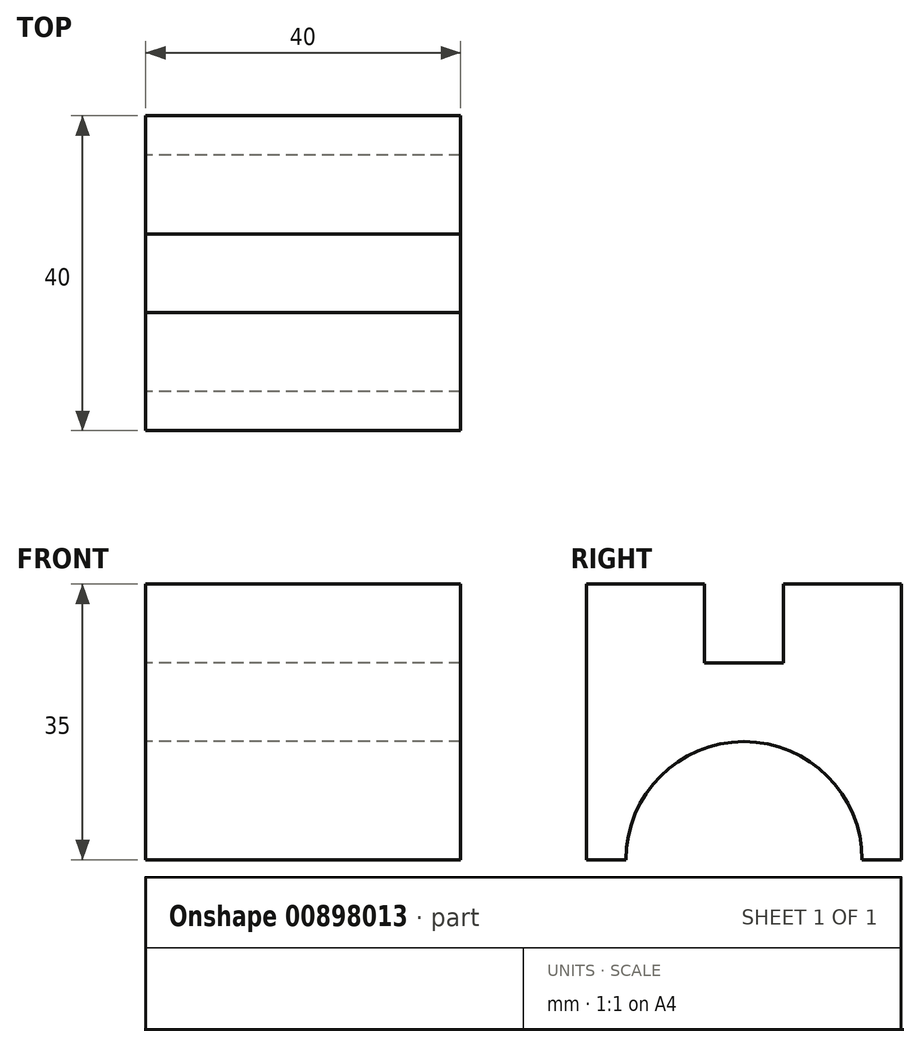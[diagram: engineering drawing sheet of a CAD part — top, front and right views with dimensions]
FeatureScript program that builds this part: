
annotation { "Feature Type Name" : "Feature", "Feature Type Description" : "" }
export const myFeature = defineFeature(function(context is Context, id is Id, definition is map)
    precondition{}
    {
        {
            var Q0;
            Q0=qCreatedBy(makeId("Front.planeOp"),FACE);
            var sketch = newSketch(context, id + "F0", { "sketchPlane" : qUnion([Q0])});
            skLineSegment(sketch, "E0.bottom", {"start": v(-20, 35) * mm, "end": v(20, 35) * mm});
            skLineSegment(sketch, "E0.top", {"start": v(-20, 0) * mm, "end": v(20, 0) * mm});
            skLineSegment(sketch, "E0.left", {"start": v(-20, 35) * mm, "end": v(-20, 0) * mm});
            skLineSegment(sketch, "E0.right", {"start": v(20, 35) * mm, "end": v(20, 0) * mm});
            skSolve(sketch);
        }
        {
            var Q0;
            Q0=makeQuery(id+"F0.imprint","IMPRINT",FACE,{"disambiguationData":[TD([[makeQuery(id+"F0.imprint","IMPRINT",EDGE,{"derivedFrom":sQuery(id+"F0.wireOp",EDGE,"E0.bottom")}),-1.0]])]});
            extrude(context, id + "F1", {"entities" : qUnion([Q0]), "endBound" : BoundingType.SYMMETRIC, "depth" : 40 * mm, "offsetDistance" : 25 * mm});
        }
        {
            var Q0;
            Q0=makeQuery(id+"F1.opExtrude","SWEPT_FACE",FACE,{"disambiguationData":[OSD([sQuery(id+"F0.wireOp",EDGE,"E0.left")])]});
            var sketch = newSketch(context, id + "F2", { "sketchPlane" : qUnion([Q0])});
            skCircle(sketch, "E1", {"center": v(0, 0) * mm, "radius": 15 * mm});
            skLineSegment(sketch, "E2.bottom", {"start": v(-5, 35) * mm, "end": v(5, 35) * mm});
            skLineSegment(sketch, "E2.top", {"start": v(-5, 25) * mm, "end": v(5, 25) * mm});
            skLineSegment(sketch, "E2.left", {"start": v(-5, 35) * mm, "end": v(-5, 25) * mm});
            skLineSegment(sketch, "E2.right", {"start": v(5, 35) * mm, "end": v(5, 25) * mm});
            skSolve(sketch);
        }
        {
            var Q0;
            {var subQ0=sQuery(id+"F2.wireOp",EDGE,"E1");var subQ1=makeQuery(id+"F1.opExtrude","SWEPT_EDGE",EDGE,{"disambiguationData":[OSD([sQuery(id+"F0.wireOp",EDGE,"E0.top"),sQuery(id+"F0.wireOp",EDGE,"E0.left")])]});var subQ2=makeQuery(id+"F2.imprint","INTERSECT",VERTEX,{"disambiguationData":[OD(0.0)],"derivedFrom":[subQ1,subQ0]});Q0=makeQuery(id+"F2.imprint","IMPRINT",FACE,{"disambiguationData":[TD([[makeQuery(id+"F2.imprint","IMPRINT",EDGE,{"disambiguationData":[TD([[subQ2,1.0]])],"derivedFrom":subQ0}),1.0]])]});}
            extrude(context, id + "F3", {"entities" : qUnion([Q0]), "operationType" : NewBodyOperationType.REMOVE, "endBound" : BoundingType.SYMMETRIC, "oppositeDirection" : true, "depth" : 200 * mm, "offsetDistance" : 25 * mm});
        }
        {
            var Q0;
            Q0=makeQuery(id+"F2.imprint","IMPRINT",FACE,{"disambiguationData":[TD([[makeQuery(id+"F2.imprint","IMPRINT",EDGE,{"derivedFrom":sQuery(id+"F2.wireOp",EDGE,"E2.bottom")}),1.0]])]});
            extrude(context, id + "F4", {"entities" : qUnion([Q0]), "operationType" : NewBodyOperationType.REMOVE, "endBound" : BoundingType.THROUGH_ALL, "oppositeDirection" : true, "depth" : 25 * mm, "offsetDistance" : 25 * mm});
        }
    });
